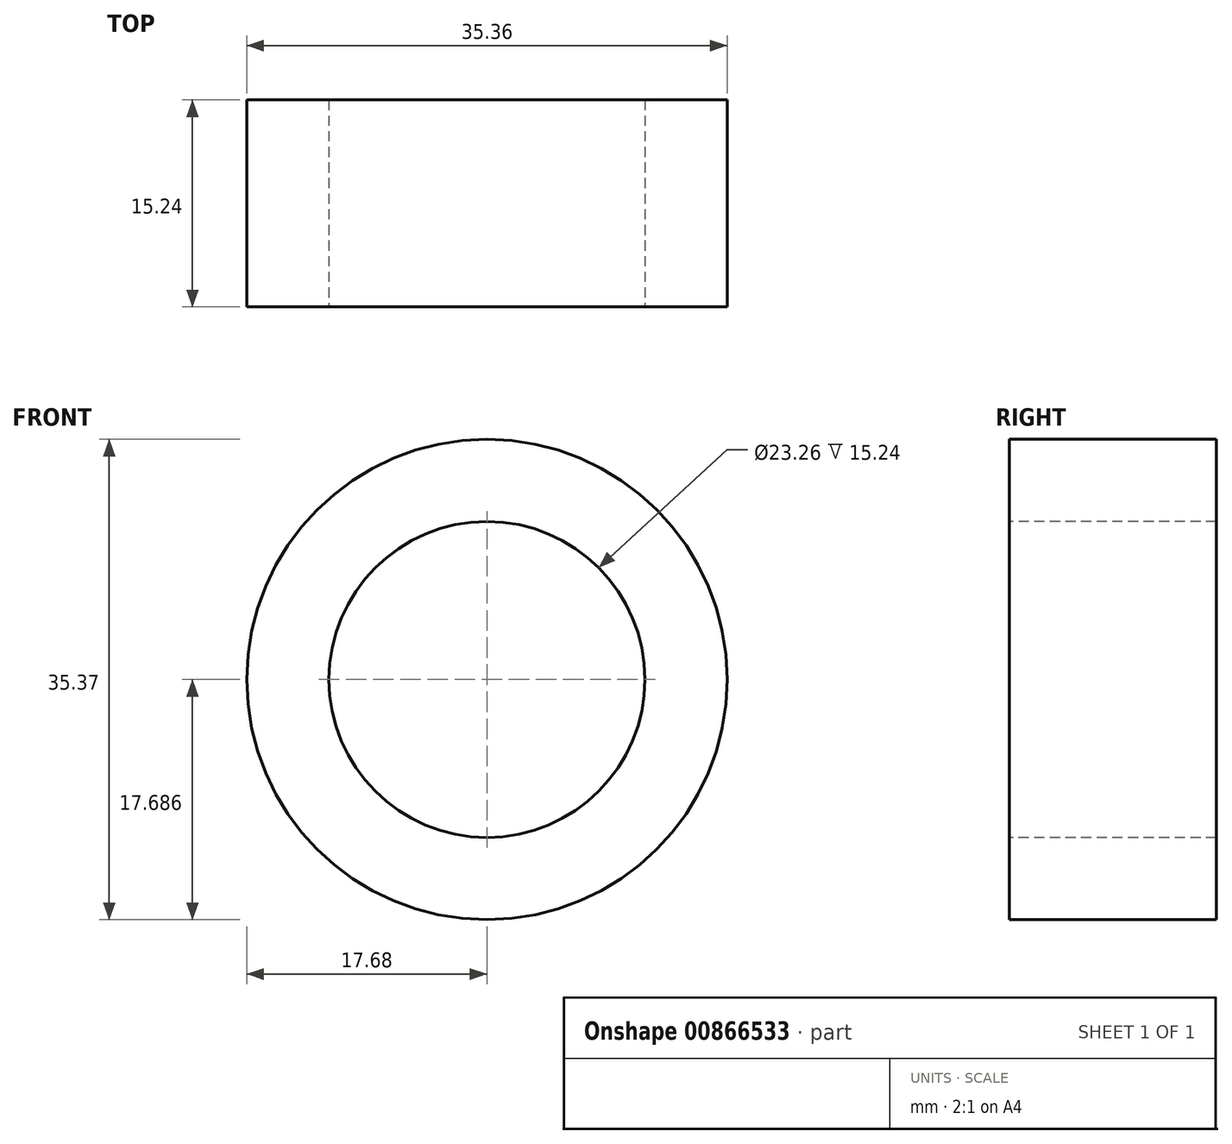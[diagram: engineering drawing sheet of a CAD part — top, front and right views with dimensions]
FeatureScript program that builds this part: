
annotation { "Feature Type Name" : "Feature", "Feature Type Description" : "" }
export const myFeature = defineFeature(function(context is Context, id is Id, definition is map)
    precondition{}
    {
        {
            var Q0;
            Q0=qCreatedBy(makeId("Front.planeOp"),FACE);
            var sketch = newSketch(context, id + "F0", { "sketchPlane" : qUnion([Q0])});
            skLineSegment(sketch, "E0", {"start": v(-8.03, 6.86) * mm, "end": v(-8.03, -49.57) * mm});
            skLineSegment(sketch, "E1", {"start": v(-1.68, -55.92) * mm, "end": v(1.68, -55.92) * mm});
            skLineSegment(sketch, "E2", {"start": v(8.03, -49.57) * mm, "end": v(8.03, 6.57) * mm});
            skPoint(sketch, "E3.visualSharp", {"position": v(-8.03, -55.92) * mm});
            skArc(sketch, "E3.filletArc", {"start": v(-8.03, -49.57) * mm, "mid": v(-6.17, -54.06) * mm, "end": v(-1.68, -55.92) * mm});
            skPoint(sketch, "E4.visualSharp", {"position": v(8.03, -55.92) * mm});
            skArc(sketch, "E4.filletArc", {"start": v(1.68, -55.92) * mm, "mid": v(6.17, -54.06) * mm, "end": v(8.03, -49.57) * mm});
            skLineSegment(sketch, "E5", {"start": v(-8.03, 6.86) * mm, "end": v(-5.4, 34.33) * mm});
            skLineSegment(sketch, "E6", {"start": v(8.03, 6.57) * mm, "end": v(4.23, 34.02) * mm});
            skCircle(sketch, "E7", {"center": v(0, 51.86) * mm, "radius": 17.68 * mm});
            skSolve(sketch);
        }
        {
            var Q0;
            Q0 = qSketchRegion(id + "F0", true);
            extrude(context, id + "F1", {"entities" : qUnion([Q0]), "depth" : 15.24 * mm, "offsetDistance" : 25.4 * mm});
        }
        {
            var Q0;
            Q0=sQuery(id+"F0.wireOp",EDGE,"E5");
            var Q1;
            Q1=sQuery(id+"F0.wireOp",EDGE,"E0");
            var Q2;
            Q2=sQuery(id+"F0.wireOp",EDGE,"E3.filletArc");
            var Q3;
            Q3=sQuery(id+"F0.wireOp",EDGE,"E1");
            var Q4;
            Q4=sQuery(id+"F0.wireOp",EDGE,"E4.filletArc");
            var Q5;
            Q5=sQuery(id+"F0.wireOp",EDGE,"E2");
            var Q6;
            Q6=sQuery(id+"F0.wireOp",EDGE,"E6");
            extrude(context, id + "F2", {"bodyType" : ToolBodyType.SURFACE, "surfaceEntities" : qUnion([Q0, Q1, Q2, Q3, Q4, Q5, Q6]), "depth" : 15.24 * mm, "offsetDistance" : 25.4 * mm});
        }
        {
            var Q0;
            Q0=makeQuery(id+"F1.opExtrude","CAP_FACE",FACE,{"disambiguationData":[OSD([sQuery(id+"F0.wireOp",EDGE,"E7")])],"isStart":false});
            var sketch = newSketch(context, id + "F3", { "sketchPlane" : qUnion([Q0])});
            skCircle(sketch, "E8", {"center": v(0, 51.86) * mm, "radius": 11.63 * mm});
            skSolve(sketch);
        }
        {
            var Q0;
            Q0 = qSketchRegion(id + "F3", true);
            extrude(context, id + "F4", {"entities" : qUnion([Q0]), "operationType" : NewBodyOperationType.REMOVE, "oppositeDirection" : true, "depth" : 15.24 * mm, "offsetDistance" : 25.4 * mm});
        }
    });
